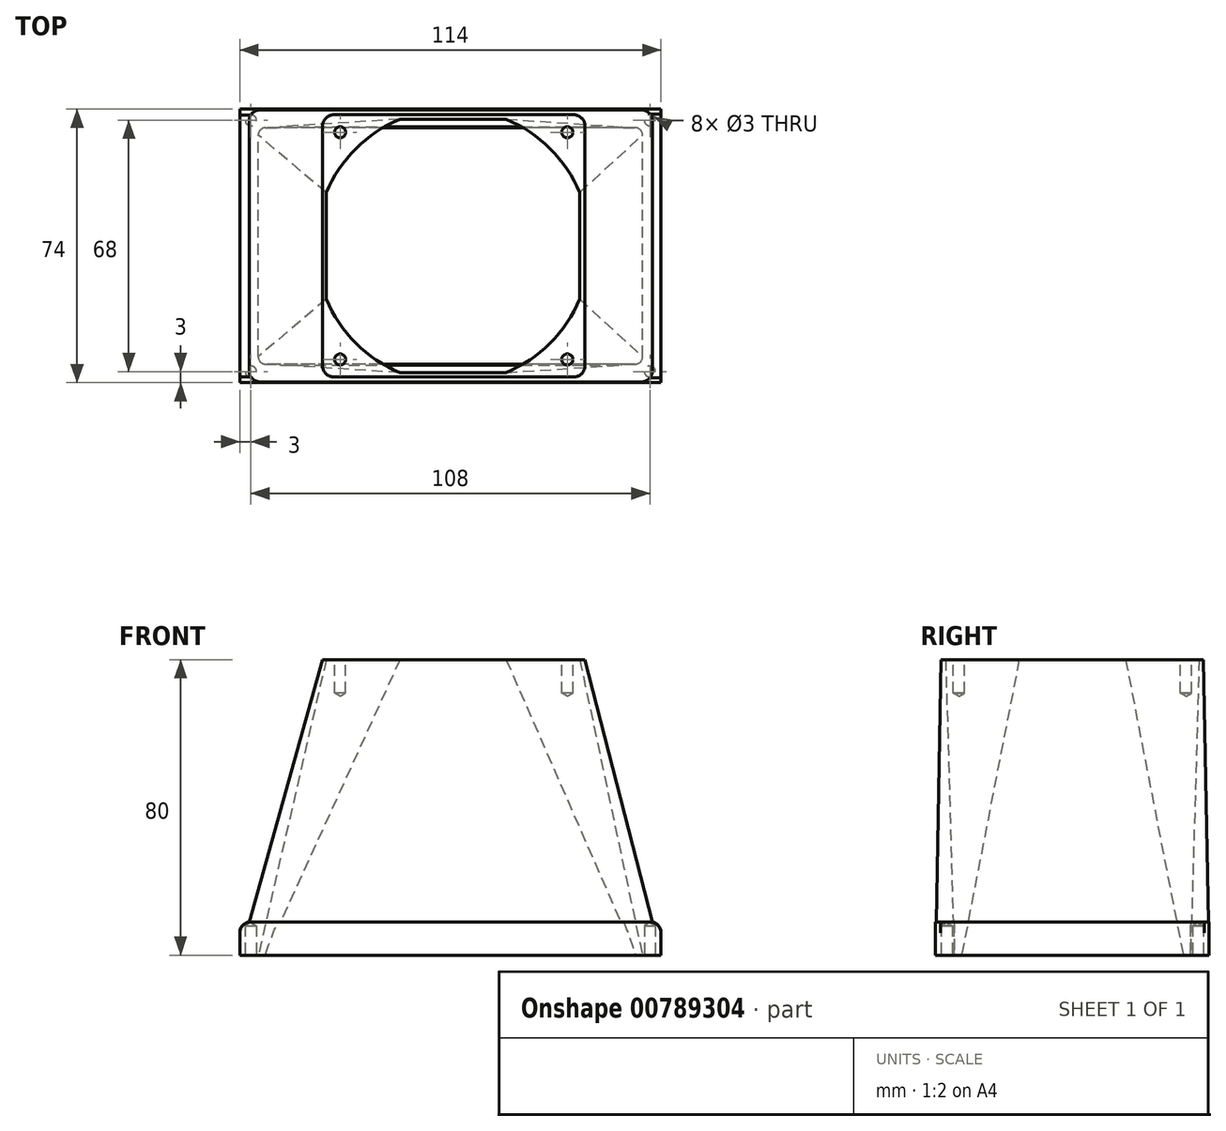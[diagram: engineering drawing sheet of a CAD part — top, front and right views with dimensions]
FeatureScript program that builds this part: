
annotation { "Feature Type Name" : "Feature", "Feature Type Description" : "" }
export const myFeature = defineFeature(function(context is Context, id is Id, definition is map)
    precondition{}
    {
        {
            var Q0;
            Q0=qCreatedBy(makeId("Top.planeOp"),FACE);
            var sketch = newSketch(context, id + "F0", { "sketchPlane" : qUnion([Q0])});
            skLineSegment(sketch, "E0.bottom", {"start": v(-2, 0) * mm, "end": v(-102, 0) * mm});
            skLineSegment(sketch, "E0.top", {"start": v(-2, 64) * mm, "end": v(-102, 64) * mm});
            skLineSegment(sketch, "E0.left", {"start": v(0, 2) * mm, "end": v(0, 62) * mm});
            skLineSegment(sketch, "E0.right", {"start": v(-104, 2) * mm, "end": v(-104, 62) * mm});
            skLineSegment(sketch, "E1.0", {"start": v(-109, -5) * mm, "end": v(-109, 69) * mm});
            skLineSegment(sketch, "E1.1", {"start": v(5, -5) * mm, "end": v(-109, -5) * mm});
            skLineSegment(sketch, "E1.2", {"start": v(5, -5) * mm, "end": v(5, 69) * mm});
            skLineSegment(sketch, "E1.3", {"start": v(5, 69) * mm, "end": v(-109, 69) * mm});
            skPoint(sketch, "E2.visualSharp", {"position": v(-104, 64) * mm});
            skArc(sketch, "E2.filletArc", {"start": v(-102, 64) * mm, "mid": v(-103.41, 63.41) * mm, "end": v(-104, 62) * mm});
            skPoint(sketch, "E3.visualSharp", {"position": v(0, 64) * mm});
            skArc(sketch, "E3.filletArc", {"start": v(0, 62) * mm, "mid": v(-0.59, 63.41) * mm, "end": v(-2, 64) * mm});
            skPoint(sketch, "E4.visualSharp", {"position": v(0, 0) * mm});
            skArc(sketch, "E4.filletArc", {"start": v(-2, 0) * mm, "mid": v(-0.59, 0.59) * mm, "end": v(0, 2) * mm});
            skPoint(sketch, "E5.visualSharp", {"position": v(-104, 0) * mm});
            skArc(sketch, "E5.filletArc", {"start": v(-104, 2) * mm, "mid": v(-103.41, 0.59) * mm, "end": v(-102, 0) * mm});
            skSolve(sketch);
        }
        {
            var Q0;
            Q0=qCreatedBy(makeId("Top.planeOp"),FACE);
            cPlane(context, id + "F1", {"entities" : qUnion([Q0]), "cplaneType" : CPlaneType.OFFSET, "offset" : 80 * mm, "width" : 150 * mm, "height" : 150 * mm});
        }
        {
            var Q0;
            Q0=qCreatedBy(id+"F1.planeOp",FACE);
            var sketch = newSketch(context, id + "F2", { "sketchPlane" : qUnion([Q0])});
            skLineSegment(sketch, "E6.bottom", {"start": v(-65.7, 66.3) * mm, "end": v(-36.9, 66.3) * mm});
            skLineSegment(sketch, "E6.top", {"start": v(-65.7, -2.3) * mm, "end": v(-36.9, -2.3) * mm});
            skLineSegment(sketch, "E6.left", {"start": v(-85.6, 46.4) * mm, "end": v(-85.6, 17.6) * mm});
            skLineSegment(sketch, "E6.right", {"start": v(-17, 46.4) * mm, "end": v(-17, 17.6) * mm});
            skArc(sketch, "E7", {"start": v(-65.7, 66.3) * mm, "mid": v(-77.6, 58.3) * mm, "end": v(-85.6, 46.4) * mm});
            skPoint(sketch, "E8", {"position": v(-65.7, 66.3) * mm});
            skPoint(sketch, "E9", {"position": v(-85.6, 46.4) * mm});
            skPoint(sketch, "E10", {"position": v(-85.6, 17.6) * mm});
            skPoint(sketch, "E11", {"position": v(-65.7, -2.3) * mm});
            skPoint(sketch, "E12", {"position": v(-36.9, -2.3) * mm});
            skPoint(sketch, "E13", {"position": v(-17, 17.6) * mm});
            skPoint(sketch, "E14", {"position": v(-17, 46.4) * mm});
            skPoint(sketch, "E15", {"position": v(-36.9, 66.3) * mm});
            skArc(sketch, "E16.trimOffspring", {"start": v(-17, 46.4) * mm, "mid": v(-25, 58.3) * mm, "end": v(-36.9, 66.3) * mm});
            skArc(sketch, "E17.trimOffspring", {"start": v(-36.9, -2.3) * mm, "mid": v(-25, 5.7) * mm, "end": v(-17, 17.6) * mm});
            skArc(sketch, "E18.trimOffspring", {"start": v(-85.6, 17.6) * mm, "mid": v(-77.6, 5.7) * mm, "end": v(-65.7, -2.3) * mm});
            skLineSegment(sketch, "E19.bottom", {"start": v(-86.8, 67.5) * mm, "end": v(-15.8, 67.5) * mm});
            skLineSegment(sketch, "E19.top", {"start": v(-86.8, -3.5) * mm, "end": v(-15.8, -3.5) * mm});
            skLineSegment(sketch, "E19.left", {"start": v(-86.8, 67.5) * mm, "end": v(-86.8, -3.5) * mm});
            skLineSegment(sketch, "E19.right", {"start": v(-15.8, 67.5) * mm, "end": v(-15.8, -3.5) * mm});
            skLineSegment(sketch, "E20.0", {"start": v(0, 2) * mm, "end": v(0, 62) * mm});
            skSolve(sketch);
        }
        {
            var Q0;
            Q0=qCreatedBy(id+"F1.planeOp",FACE);
            var sketch = newSketch(context, id + "F3", { "sketchPlane" : qUnion([Q0])});
            skPoint(sketch, "E21", {"position": v(-65.48, 74.41) * mm});
            skPoint(sketch, "E22", {"position": v(-85.38, 54.51) * mm});
            skPoint(sketch, "E23", {"position": v(-85.38, 25.71) * mm});
            skPoint(sketch, "E24", {"position": v(-65.48, 5.81) * mm});
            skPoint(sketch, "E25", {"position": v(-36.68, 5.81) * mm});
            skPoint(sketch, "E26", {"position": v(-16.78, 25.71) * mm});
            skPoint(sketch, "E27", {"position": v(-16.78, 54.51) * mm});
            skPoint(sketch, "E28", {"position": v(-36.68, 74.41) * mm});
            skLineSegment(sketch, "E29.bottom", {"start": v(-86.6, 67.5) * mm, "end": v(-15.6, 67.5) * mm});
            skLineSegment(sketch, "E29.top", {"start": v(-86.6, -3.5) * mm, "end": v(-15.6, -3.5) * mm});
            skLineSegment(sketch, "E29.left", {"start": v(-86.6, 67.5) * mm, "end": v(-86.6, -3.5) * mm});
            skLineSegment(sketch, "E29.right", {"start": v(-15.6, 67.5) * mm, "end": v(-15.6, -3.5) * mm});
            skLineSegment(sketch, "E30.0", {"start": v(0.22, -38.45) * mm, "end": v(0.22, 36.55) * mm});
            skSolve(sketch);
        }
        {
            var Q0;
            Q0=qCreatedBy(makeId("Top.planeOp"),FACE);
            var sketch = newSketch(context, id + "F4", { "sketchPlane" : qUnion([Q0])});
            skLineSegment(sketch, "E31.0", {"start": v(-109, -5) * mm, "end": v(-109, 69) * mm});
            skLineSegment(sketch, "E32.0", {"start": v(5, 69) * mm, "end": v(-109, 69) * mm});
            skLineSegment(sketch, "E33.0", {"start": v(5, -5) * mm, "end": v(5, 69) * mm});
            skLineSegment(sketch, "E34.0", {"start": v(5, -5) * mm, "end": v(-109, -5) * mm});
            skSolve(sketch);
        }
        {
            var Q0;
            Q0=makeQuery(id+"F4.imprint","IMPRINT",FACE,{"disambiguationData":[TD([[makeQuery(id+"F4.imprint","IMPRINT",EDGE,{"derivedFrom":sQuery(id+"F4.wireOp",EDGE,"E31.0")}),-1.0]])]});
            var Q1;
            Q1=makeQuery(id+"F3.imprint","IMPRINT",FACE,{"disambiguationData":[TD([[makeQuery(id+"F3.imprint","IMPRINT",EDGE,{"derivedFrom":sQuery(id+"F3.wireOp",EDGE,"E29.bottom")}),-1.0]])]});
            loft(context, id + "F5", {"sheetProfilesArray" : [{ "sheetProfileEntities" : qUnion([Q0]) }, { "sheetProfileEntities" : qUnion([Q1]) }], "trimGuidesByProfiles" : true});
        }
        {
            var Q0;
            Q0=makeQuery(id+"F2.imprint","IMPRINT",FACE,{"disambiguationData":[TD([[makeQuery(id+"F2.imprint","IMPRINT",EDGE,{"derivedFrom":sQuery(id+"F2.wireOp",EDGE,"E6.bottom")}),-1.0]])]});
            var Q1;
            Q1=makeQuery(id+"F0.imprint","IMPRINT",FACE,{"disambiguationData":[TD([[makeQuery(id+"F0.imprint","IMPRINT",EDGE,{"derivedFrom":sQuery(id+"F0.wireOp",EDGE,"E0.bottom")}),-1.0]])]});
            var Q2;
            Q2=makeQuery(id+"F2.imprint","IMPRINT",FACE,{"disambiguationData":[TD([[makeQuery(id+"F2.imprint","IMPRINT",EDGE,{"derivedFrom":sQuery(id+"F2.wireOp",EDGE,"E6.bottom")}),-1.0]])]});
            var Q3;
            Q3=makeQuery(id+"F0.imprint","IMPRINT",FACE,{"disambiguationData":[TD([[makeQuery(id+"F0.imprint","IMPRINT",EDGE,{"derivedFrom":sQuery(id+"F0.wireOp",EDGE,"E0.bottom")}),-1.0]])]});
            loft(context, id + "F6", {"operationType" : NewBodyOperationType.REMOVE, "sheetProfilesArray" : [{ "sheetProfileEntities" : qUnion([Q0]) }, { "sheetProfileEntities" : qUnion([Q1]) }], "wireProfilesArray" : [{ "wireProfileEntities" : qUnion([Q2]) }, { "wireProfileEntities" : qUnion([Q3]) }]});
        }
        {
            var Q0;
            Q0=makeQuery(id+"F5.opLoft","CAP_FACE",FACE,{"disambiguationData":[OSD([makeQuery(id+"F3.imprint","IMPRINT",FACE,{"disambiguationData":[TD([[makeQuery(id+"F3.imprint","IMPRINT",EDGE,{"derivedFrom":sQuery(id+"F3.wireOp",EDGE,"E29.bottom")}),-1.0]])]})])],"isStart":true});
            var sketch = newSketch(context, id + "F7", { "sketchPlane" : qUnion([Q0])});
            skLineSegment(sketch, "E35.0", {"start": v(-86.6, -3.5) * mm, "end": v(-15.6, -3.5) * mm});
            skLineSegment(sketch, "E36.0", {"start": v(-86.6, 67.5) * mm, "end": v(-86.6, -3.5) * mm});
            skLineSegment(sketch, "E37.0", {"start": v(-15.6, 67.5) * mm, "end": v(-86.6, 67.5) * mm});
            skLineSegment(sketch, "E38.0", {"start": v(-15.6, -3.5) * mm, "end": v(-15.6, 67.5) * mm});
            skCircle(sketch, "E39", {"center": v(-81.84, 1.25) * mm, "radius": 2.15 * mm});
            skCircle(sketch, "E40.0.1.0", {"center": v(-81.84, 62.75) * mm, "radius": 2.15 * mm});
            skCircle(sketch, "E40.1.0.0", {"center": v(-20.34, 1.25) * mm, "radius": 2.15 * mm});
            skCircle(sketch, "E40.1.1.0", {"center": v(-20.34, 62.75) * mm, "radius": 2.15 * mm});
            skLineSegment(sketch, "E40.direction1", {"start": v(-81.84, 1.25) * mm, "end": v(-20.34, 1.25) * mm, "construction": true});
            skLineSegment(sketch, "E40.direction2", {"start": v(-81.84, 1.25) * mm, "end": v(-81.84, 62.75) * mm, "construction": true});
            skSolve(sketch);
        }
        {
            var Q0;
            Q0=sQuery(id+"F7.wireOp",VERTEX,"E40.direction1.start");
            var Q1;
            Q1=sQuery(id+"F7.wireOp",VERTEX,"E40.direction2.end");
            var Q2;
            Q2=sQuery(id+"F7.wireOp",VERTEX,"E40.1.1.0.center");
            var Q3;
            Q3=sQuery(id+"F7.wireOp",VERTEX,"E40.direction1.end");
            var Q4;
            Q4=makeQuery(id+"F5.opLoft","SWEPT_BODY",BODY,{"disambiguationData":[OSD([makeQuery(id+"F3.imprint","IMPRINT",FACE,{"disambiguationData":[TD([[makeQuery(id+"F3.imprint","IMPRINT",EDGE,{"derivedFrom":sQuery(id+"F3.wireOp",EDGE,"E29.bottom")}),-1.0]])]}),makeQuery(id+"F4.imprint","IMPRINT",FACE,{"disambiguationData":[TD([[makeQuery(id+"F4.imprint","IMPRINT",EDGE,{"derivedFrom":sQuery(id+"F4.wireOp",EDGE,"E31.0")}),-1.0]])]})])]});
            hole(context, id + "F8", {"style" : HoleStyle.SIMPLE, "endStyle" : HoleEndStyle.BLIND, "holeDiameter" : 3 * mm, "majorDiameter" : 5 * mm, "holeDepth" : 9 * mm, "isTappedThrough" : true, "tappedDepth" : 12 * mm, "tapClearance" : 3, "startFromSketch" : true, "locations" : qUnion([Q0, Q1, Q2, Q3]), "scope" : qUnion([Q4])});
        }
        {
            var Q0;
            Q0=makeQuery(id+"F0.imprint","IMPRINT",FACE,{"disambiguationData":[TD([[makeQuery(id+"F0.imprint","IMPRINT",EDGE,{"derivedFrom":sQuery(id+"F0.wireOp",EDGE,"E0.bottom")}),1.0]])]});
            extrude(context, id + "F9", {"entities" : qUnion([Q0]), "operationType" : NewBodyOperationType.ADD, "depth" : 9 * mm, "offsetDistance" : 25 * mm});
        }
        {
            var Q0;
            Q0=makeQuery(id+"F0.imprint","IMPRINT",FACE,{"disambiguationData":[TD([[makeQuery(id+"F0.imprint","IMPRINT",EDGE,{"derivedFrom":sQuery(id+"F0.wireOp",EDGE,"E0.bottom")}),1.0]])]});
            var sketch = newSketch(context, id + "F10", { "sketchPlane" : qUnion([Q0])});
            skPoint(sketch, "E41", {"position": v(-106, -2) * mm});
            skPoint(sketch, "E42.0.1.0", {"position": v(-106, 66) * mm});
            skPoint(sketch, "E42.1.0.0", {"position": v(2, -2) * mm});
            skPoint(sketch, "E42.1.1.0", {"position": v(2, 66) * mm});
            skLineSegment(sketch, "E42.direction1", {"start": v(-106, -2) * mm, "end": v(2, -2) * mm, "construction": true});
            skLineSegment(sketch, "E42.direction2", {"start": v(-106, -2) * mm, "end": v(-106, 66) * mm, "construction": true});
            skSolve(sketch);
        }
        {
            var Q0;
            Q0=sQuery(id+"F10.wireOp",VERTEX,"E41");
            var Q1;
            Q1=sQuery(id+"F10.wireOp",VERTEX,"E42.1.0.0");
            var Q2;
            Q2=sQuery(id+"F10.wireOp",VERTEX,"E42.1.1.0");
            var Q3;
            Q3=sQuery(id+"F10.wireOp",VERTEX,"E42.0.1.0");
            var Q4;
            Q4=makeQuery(id+"F5.opLoft","SWEPT_BODY",BODY,{"disambiguationData":[OSD([makeQuery(id+"F3.imprint","IMPRINT",FACE,{"disambiguationData":[TD([[makeQuery(id+"F3.imprint","IMPRINT",EDGE,{"derivedFrom":sQuery(id+"F3.wireOp",EDGE,"E29.bottom")}),-1.0]])]}),makeQuery(id+"F4.imprint","IMPRINT",FACE,{"disambiguationData":[TD([[makeQuery(id+"F4.imprint","IMPRINT",EDGE,{"derivedFrom":sQuery(id+"F4.wireOp",EDGE,"E31.0")}),-1.0]])]})])]});
            hole(context, id + "F11", {"style" : HoleStyle.SIMPLE, "endStyle" : HoleEndStyle.BLIND, "oppositeDirection" : true, "holeDiameter" : 3 * mm, "majorDiameter" : 5 * mm, "holeDepth" : 8 * mm, "isTappedThrough" : true, "tappedDepth" : 12 * mm, "tapClearance" : 3, "startFromSketch" : true, "locations" : qUnion([Q0, Q1, Q2, Q3]), "scope" : qUnion([Q4])});
        }
        {
            var Q0;
            Q0=makeQuery(id+"F5.opLoft","SWEPT_EDGE",EDGE,{"disambiguationData":[OSD([sQuery(id+"F3.wireOp",EDGE,"E29.top"),sQuery(id+"F3.wireOp",EDGE,"E29.right"),sQuery(id+"F4.wireOp",EDGE,"E33.0"),sQuery(id+"F4.wireOp",EDGE,"E34.0")])]});
            var Q1;
            Q1=makeQuery(id+"F5.opLoft","SWEPT_EDGE",EDGE,{"disambiguationData":[OSD([sQuery(id+"F3.wireOp",EDGE,"E29.top"),sQuery(id+"F3.wireOp",EDGE,"E29.left"),sQuery(id+"F4.wireOp",EDGE,"E31.0"),sQuery(id+"F4.wireOp",EDGE,"E34.0")])]});
            var Q2;
            Q2=makeQuery(id+"F5.opLoft","SWEPT_EDGE",EDGE,{"disambiguationData":[OSD([sQuery(id+"F3.wireOp",EDGE,"E29.bottom"),sQuery(id+"F3.wireOp",EDGE,"E29.left"),sQuery(id+"F4.wireOp",EDGE,"E31.0"),sQuery(id+"F4.wireOp",EDGE,"E32.0")])]});
            var Q3;
            Q3=makeQuery(id+"F5.opLoft","SWEPT_EDGE",EDGE,{"disambiguationData":[OSD([sQuery(id+"F3.wireOp",EDGE,"E29.bottom"),sQuery(id+"F3.wireOp",EDGE,"E29.right"),sQuery(id+"F4.wireOp",EDGE,"E32.0"),sQuery(id+"F4.wireOp",EDGE,"E33.0")])]});
            fillet(context, id + "F12", {"entities" : qUnion([Q0, Q1, Q2, Q3]), "radius" : 3 * mm, "tangentPropagation" : true, "allowEdgeOverflow" : false});
        }
        {
            var Q0;
            Q0=makeQuery(id+"F9.opExtrude","CAP_EDGE",EDGE,{"disambiguationData":[OSD([sQuery(id+"F0.wireOp",EDGE,"E1.0")])],"isStart":false});
            var Q1;
            Q1=makeQuery(id+"F9.opExtrude","CAP_EDGE",EDGE,{"disambiguationData":[OSD([sQuery(id+"F0.wireOp",EDGE,"E1.2")])],"isStart":false});
            fillet(context, id + "F13", {"entities" : qUnion([Q0, Q1]), "radius" : 3 * mm, "tangentPropagation" : true, "allowEdgeOverflow" : false});
        }
    });
